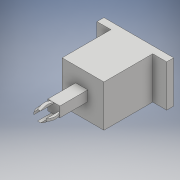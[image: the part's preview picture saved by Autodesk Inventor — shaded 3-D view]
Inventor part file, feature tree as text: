
AUTODESK INVENTOR PART (.ipt)
format: ipt  version: 2018 (Build 220112000, 112)  size: 168,960 bytes
history: native  units: mm
features: extrude x7, sketch x7
ambient origin geometry x8: Origin, YZ Plane, XZ Plane, XY Plane, X Axis, Y Axis, Z Axis, Center Point
bodies: Solid1 (feature_tree)
feature tree (14):
  extrude  "Extrusion1"  Depth=10.0mm
  extrude  "Extrusion2"  Depth=70.0mm
  extrude  "Extrusion3"  Depth=40.0mm TaperAngle=0.0deg
  extrude  "Extrusion4"  Depth=20.0mm TaperAngle=0.0deg
  extrude  "Extrusion5"  Depth=20.0mm TaperAngle=0.0deg
  extrude  "Extrusion6"  [1 undecoded]
  extrude  "Extrusion7"  [1 undecoded]
  sketch  "Sketch1"  dims[d0=100.0mm d1=10.0mm]
  sketch  "Sketch3"  dims[d2=60.0mm d3=70.0mm]
  sketch  "Sketch4"  dims[d4=60.0mm d5=0.0mm d6=40.0mm d7=0.0mm]
  sketch  "Sketch9"  dims[d8=20.0mm d9=0.0mm d11=20.0mm d12=0.0mm]
  sketch  "Sketch10"  dims[d13=20.0mm d14=0.0mm d15=20.0mm d16=0.0mm]
  sketch  "Sketch11"  dims[d17=20.0mm d18=0.0mm]
  sketch  "Sketch12"
note: 2 required parameter values undecoded (feature->parameter linkage not recoverable at this tier; creation-order binding heuristic only, values carry confidence <= 0.55)
